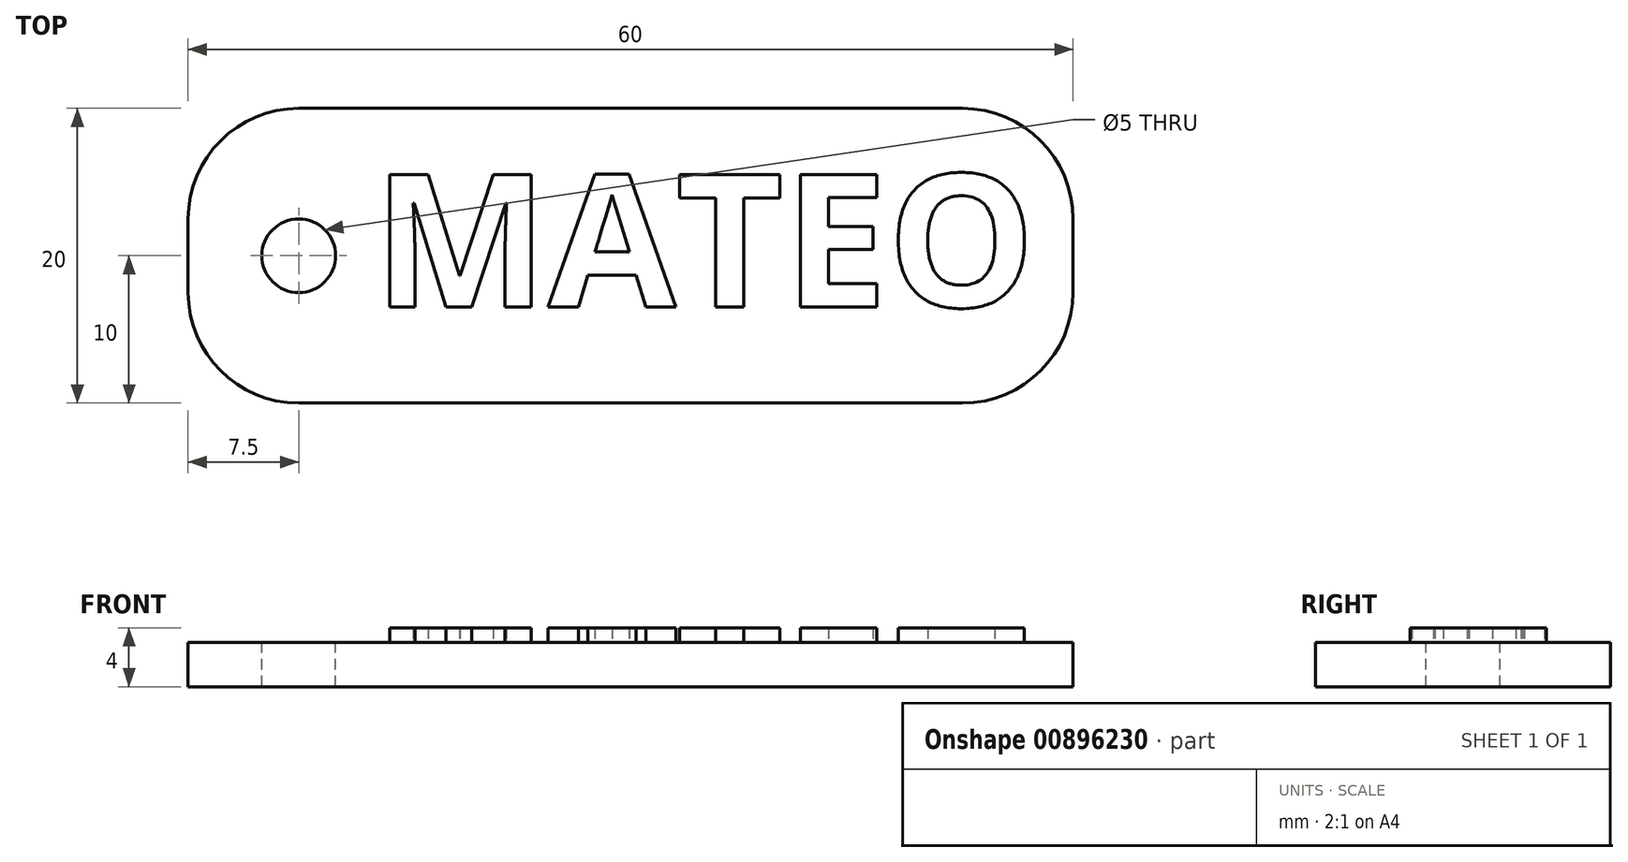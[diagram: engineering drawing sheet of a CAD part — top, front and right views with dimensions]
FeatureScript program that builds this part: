
annotation { "Feature Type Name" : "Feature", "Feature Type Description" : "" }
export const myFeature = defineFeature(function(context is Context, id is Id, definition is map)
    precondition{}
    {
        {
            var Q0;
            Q0=qCreatedBy(makeId("Top.planeOp"),FACE);
            var sketch = newSketch(context, id + "F0", { "sketchPlane" : qUnion([Q0])});
            skLineSegment(sketch, "E0.bottom", {"start": v(0, 0) * mm, "end": v(60, 0) * mm});
            skLineSegment(sketch, "E0.top", {"start": v(0, -20) * mm, "end": v(60, -20) * mm});
            skLineSegment(sketch, "E0.left", {"start": v(0, 0) * mm, "end": v(0, -20) * mm});
            skLineSegment(sketch, "E0.right", {"start": v(60, 0) * mm, "end": v(60, -20) * mm});
            skLineSegment(sketch, "E1", {"start": v(0, -10) * mm, "end": v(7.5, -10) * mm, "construction": true});
            skCircle(sketch, "E2", {"center": v(7.5, -10) * mm, "radius": 2.5 * mm});
            skSolve(sketch);
        }
        {
            var Q0;
            Q0=qCreatedBy(makeId("Top.planeOp"),FACE);
            var sketch = newSketch(context, id + "F1", { "sketchPlane" : qUnion([Q0])});
            skText(sketch, "E3", { "text": "MATEO", "fontName": "OpenSans-Bold.ttf"});
            const initialGuessF1  = {"E3": [0.01254, -0.01347, 1, 0, 0.00906]};
            skSetInitialGuess(sketch, initialGuessF1);
            skSolve(sketch);
        }
        {
            var Q0;
            Q0=makeQuery(id+"F0.imprint","IMPRINT",FACE,{"disambiguationData":[TD([[makeQuery(id+"F0.imprint","IMPRINT",EDGE,{"derivedFrom":sQuery(id+"F0.wireOp",EDGE,"E0.bottom")}),-1.0]])]});
            extrude(context, id + "F2", {"entities" : qUnion([Q0]), "oppositeDirection" : true, "depth" : 3 * mm, "offsetDistance" : 25 * mm});
        }
        {
            var Q0;
            Q0 = qSketchRegion(id + "F1", true);
            extrude(context, id + "F3", {"entities" : qUnion([Q0]), "operationType" : NewBodyOperationType.ADD, "flatOperationType" : FlatOperationType.REMOVE, "depth" : 1 * mm, "offsetDistance" : 25 * mm, "domain" : OperationDomain.MODEL});
        }
        {
            var Q0;
            Q0=makeQuery(id+"F2.opExtrude","SWEPT_EDGE",EDGE,{"disambiguationData":[OSD([sQuery(id+"F0.wireOp",EDGE,"E0.top"),sQuery(id+"F0.wireOp",EDGE,"E0.left")])]});
            var Q1;
            Q1=makeQuery(id+"F2.opExtrude","SWEPT_EDGE",EDGE,{"disambiguationData":[OSD([sQuery(id+"F0.wireOp",EDGE,"E0.top"),sQuery(id+"F0.wireOp",EDGE,"E0.right")])]});
            var Q2;
            Q2=makeQuery(id+"F2.opExtrude","SWEPT_EDGE",EDGE,{"disambiguationData":[OSD([sQuery(id+"F0.wireOp",EDGE,"E0.bottom"),sQuery(id+"F0.wireOp",EDGE,"E0.right")])]});
            var Q3;
            Q3=makeQuery(id+"F2.opExtrude","SWEPT_EDGE",EDGE,{"disambiguationData":[OSD([sQuery(id+"F0.wireOp",EDGE,"E0.bottom"),sQuery(id+"F0.wireOp",EDGE,"E0.left")])]});
            fillet(context, id + "F4", {"entities" : qUnion([Q0, Q1, Q2, Q3]), "radius" : 7.5 * mm, "tangentPropagation" : true, "allowEdgeOverflow" : false});
        }
    });
